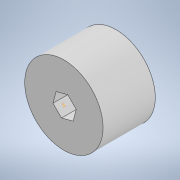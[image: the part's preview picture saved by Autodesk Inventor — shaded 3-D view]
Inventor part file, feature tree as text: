
AUTODESK INVENTOR PART (.ipt)
format: ipt  version: 2021.2 (Build 252289000, 289)  size: 134,656 bytes
history: native  units: mm
features: sketch x4, other x2, extrude x2
ambient origin geometry x8: Origin, YZ Plane, XZ Plane, XY Plane, X Axis, Y Axis, Z Axis, Center Point
bodies: Body1 (feature_tree)
feature tree (8):
  other  "Твердое тело1"
  extrude  "Выдавливание1"  Depth=15.0mm
  extrude  "Выдавливание2"  Depth=10.0mm TaperAngle=0.0deg
  sketch  "Эскиз3"
  other  "Параметрическийэлемент1:1"
  sketch  "Эскиз1"
  sketch  "Эскиз2"
  sketch  "Эскиз4"
